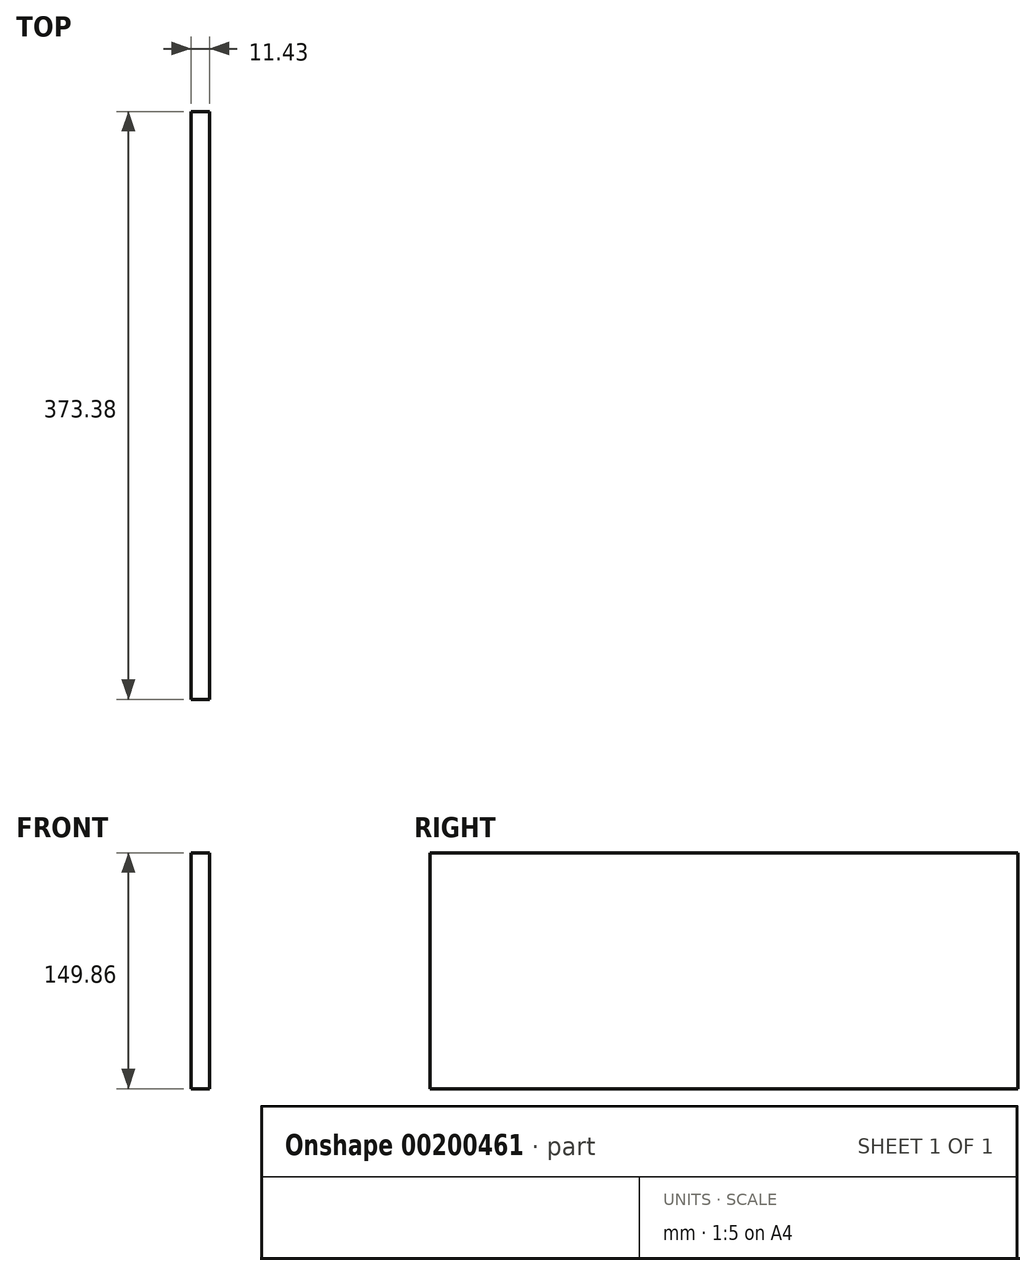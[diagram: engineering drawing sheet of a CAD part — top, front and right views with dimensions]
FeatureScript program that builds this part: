
annotation { "Feature Type Name" : "Feature", "Feature Type Description" : "" }
export const myFeature = defineFeature(function(context is Context, id is Id, definition is map)
    precondition{}
    {
        {
            var Q0;
            Q0=qCreatedBy(makeId("Right.planeOp"),FACE);
            var sketch = newSketch(context, id + "F0", { "sketchPlane" : qUnion([Q0])});
            skLineSegment(sketch, "E0.bottom", {"start": v(-498.04, 149.86) * mm, "end": v(-124.66, 149.86) * mm});
            skLineSegment(sketch, "E0.top", {"start": v(-498.04, 0) * mm, "end": v(-124.66, 0) * mm});
            skLineSegment(sketch, "E0.left", {"start": v(-498.04, 149.86) * mm, "end": v(-498.04, 0) * mm});
            skLineSegment(sketch, "E0.right", {"start": v(-124.66, 149.86) * mm, "end": v(-124.66, 0) * mm});
            skSolve(sketch);
        }
        {
            var Q0;
            Q0 = qSketchRegion(id + "F0", true);
            extrude(context, id + "F1", {"entities" : qUnion([Q0]), "depth" : 11.43 * mm});
        }
    });
